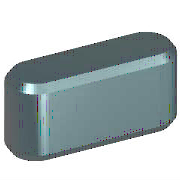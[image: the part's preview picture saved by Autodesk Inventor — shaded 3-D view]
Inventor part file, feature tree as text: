
AUTODESK INVENTOR PART (.ipt)
format: ipt  version: 2015 (Build 190159000, 159)  size: 135,168 bytes
history: native  units: mm (DEFAULTED — no unit token found)
features: plane x3, extrude x1
ambient origin geometry x8: Origin, YZ Plane, XZ Plane, XY Plane, X Axis, Y Axis, Z Axis, Center Point
bodies: Solid1 (feature_tree)
feature tree (4):
  plane  "Work Plane1"
  plane  "Work Plane2"
  extrude  "轴承体1"  Depth=3.0mm
  plane  "Work Plane3"
